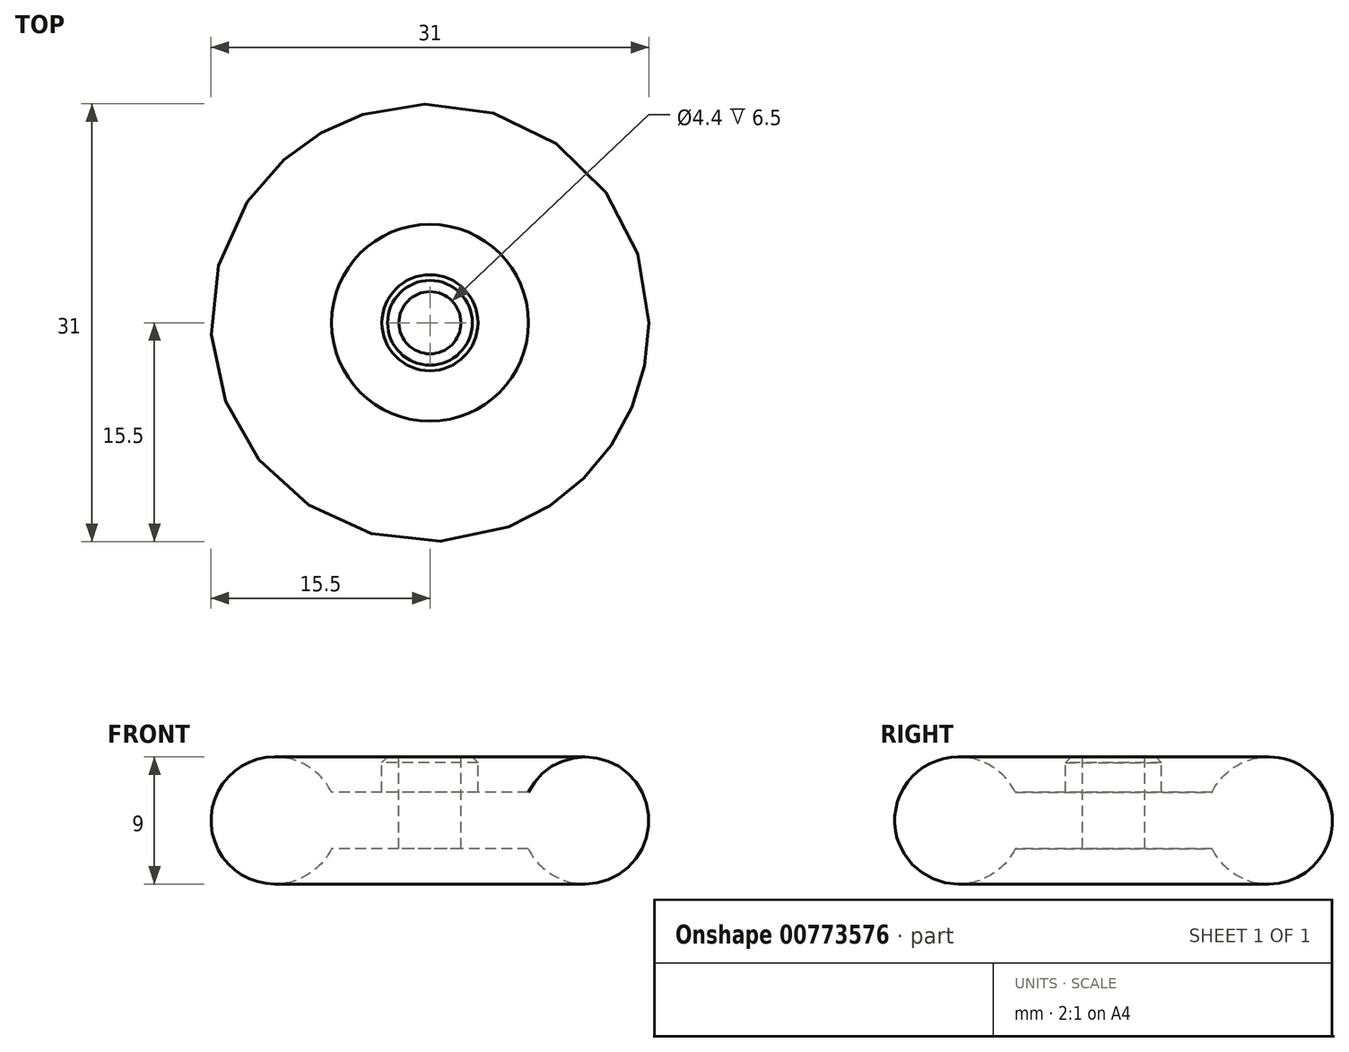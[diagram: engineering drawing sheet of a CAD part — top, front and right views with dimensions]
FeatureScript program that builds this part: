
annotation { "Feature Type Name" : "Feature", "Feature Type Description" : "" }
export const myFeature = defineFeature(function(context is Context, id is Id, definition is map)
    precondition{}
    {
        {
            var Q0;
            Q0=qCreatedBy(makeId("Front.planeOp"),FACE);
            var sketch = newSketch(context, id + "F0", { "sketchPlane" : qUnion([Q0])});
            skArc(sketch, "E0", {"start": v(6.97, -2) * mm, "mid": v(15.5, 0) * mm, "end": v(6.97, 2) * mm});
            skLineSegment(sketch, "E1", {"start": v(0, 0) * mm, "end": v(11, 0) * mm, "construction": true});
            skLineSegment(sketch, "E2", {"start": v(2.2, 6.35) * mm, "end": v(2.2, -7.01) * mm, "construction": true});
            skLineSegment(sketch, "E3", {"start": v(3.4, 2) * mm, "end": v(6.97, 2) * mm});
            skLineSegment(sketch, "E4.MirrorCS", {"start": v(2.2, -2) * mm, "end": v(6.97, -2) * mm});
            skLineSegment(sketch, "E5", {"start": v(2.2, 4.5) * mm, "end": v(3.4, 4.5) * mm});
            skLineSegment(sketch, "E6", {"start": v(3.4, 4.5) * mm, "end": v(3.4, 2) * mm});
            skLineSegment(sketch, "E7", {"start": v(2.2, -2) * mm, "end": v(2.2, 4.5) * mm});
            skPoint(sketch, "E8.orphan", {"position": v(2.2, 2) * mm});
            skLineSegment(sketch, "E9", {"start": v(0, 6.45) * mm, "end": v(0, -7.04) * mm, "construction": true});
            skLineSegment(sketch, "E10", {"start": v(-0.56, 4.5) * mm, "end": v(15.57, 4.5) * mm, "construction": true});
            skSolve(sketch);
        }
        {
            var Q0;
            Q0=makeQuery(id+"F0.imprint","IMPRINT",FACE,{"disambiguationData":[TD([[makeQuery(id+"F0.imprint","IMPRINT",EDGE,{"derivedFrom":sQuery(id+"F0.wireOp",EDGE,"E0")}),1.0]])]});
            var Q1;
            Q1=sQuery(id+"F0.wireOp",EDGE,"E9");
            revolve(context, id + "F1", {"surfaceOperationType" : NewSurfaceOperationType.NEW, "entities" : qUnion([Q0]), "axis" : qUnion([Q1]), "revolveType" : RevolveType.FULL});
        }
        {
            var Q0;
            Q0=makeQuery(id+"F1.opRevolve","SWEPT_EDGE",EDGE,{"disambiguationData":[OSD([sQuery(id+"F0.wireOp",EDGE,"E5"),sQuery(id+"F0.wireOp",EDGE,"E6")])]});
            chamfer(context, id + "F2", {"entities" : qUnion([Q0]), "width" : 0.4 * mm, "tangentPropagation" : true});
        }
    });
